# Revit family: Camera-Security-Panasonic-Super_Dynamic-Vandal_Resistant-Waterproof-Dome-Network-S2570LSeriesX
name_source: partatom
category: Security Devices
revit_build: Autodesk Revit 2016 (Build: 20150220_1215(x64)
units: mm (PartAtom-declared; Revit-internal decimal feet)

## family parameters
Cut with Voids When Loaded = No
Host = Face
Maintain Annotation Orientation = No
OmniClass Number = 23.85.10.14.11
OmniClass Title = Cameras
Part Type = Normal
Room Calculation Point = No
Round Connector Dimension = Use Diameter
Shared = No

## types (2) — shared parameters
4K = Resolution : 4K
Alarm Input Or Output Specification = ALARM IN 1(Alarm input 1/ Black & white input/ Auto time adjustment input) (x1), ALARM IN 2 (Alarm input 2/ ALARM OUT) (x1) , ALARM IN 3 (Alarm input 3/ AUX OUT) (x1)
Angle Of View = 101
Aspect169 = Yes
Audio In = Yes
Audio Out = Yes
Base Bracket Height = 1.417 "
Base Height = 2.205 "
Communication Ports = 10Base-T / 100Base-TX, RJ45 connector
Date Last Modified = 2019/05/14
Day Or Night = Yes
Decoration Cover Hole Radius = 1.634 "
Decoration Cover Wall Height = 0.118 "
Dome Bottom Offset = 0.197 "
Equipment Abbreviation = SC
Family Version = 1.0.0
Full HD = Resolution : Full HD
HD = Resolution : HD
HFOV Max 169 = 101.00°
HFOV Max 43 = 101.00°
HFOV Min 169 = 52.00°
HFOV Min 43 = 52.00°
Has POE = Yes
IP Or Analog = IP
Manufacturer = Panasonic
Minimum Illumination = 0.090 lx
Model Disclaimer = Contact Panasonic for more information
Product Documentation Link = https://bizpartner.panasonic.net
Product Page URL = https://security.panasonic.com
Provide Feedback = https://www.surveymonkey.com
Regulatory Compliance = UL (UL60950-1), c-UL (CSA C22.2 No.60950-1), CE, IEC60950-1, FCC (Part15 ClassA), ICES003 ClassA, EN55032 ClassB, EN55024
Tilt Max = 85.00°
Tilt Min = -30.00°
Tilting Range = -30 to +85
URL = http://security.panasonic.com
VFOV Max 169 = 55.00°
VFOV Max 43 = 55.00°
VFOV Min 169 = 29.00°
VFOV Min 43 = 29.00°
Vandal Resistant = Yes
Voltage DC = 12 V
WQHD = Resolution : WQHD
Wide Dynamic Range = Yes
Yaw Max = 100.00°
Yaw Min = -100.00°
Yawing Range = -100 to +100
z Const Pan Handle Length = 19.488 "
z Const Tilt Base Length = 9.843 "
z Const Tilt Base2 Length = 19.685 "
z Const Tilt Handle Length = 11.811 "
z Const Yaw Base Length = 10.236 "
z Const Yaw Base2 Length = 17.323 "
z Const Yaw Handle Length = 9.252 "
z Level Offset = 7.874 "
zero-valued in all types: Default Elevation, z Zero

## per-type parameters (varying)
- WV-S2570L: Base Radius=3.031 "; Decoration Cover Height=0.52 "; Decoration Cover Radius=4.14 "; Description=Security Camera, Fixed Dome, Network, Super Dynamic  Vandal Resistant  Weatherproof, 4K, WV-S2570L; Diameter=6.457 "; Dome Diameter=3.307 "; Height=5.472 "; Indoor Or Outdoor=Outdoor; Mounting Positions=Mount Dependent or Surface Mount; Operational Humidity=10 to 100 % (no condensation); Operational Temperature=-40 °F to 140 °F; Pan Max=180.00°; Pan Min=-180.00°; Panning Range=-180 to +180; Part Description=Security Camera, Fixed Dome, Network, Super Dynamic  Vandal Resistant  Weatherproof, 4K, WV-S2570L; Power Active=10.6 W; Product Material=Paint - Panasonic - Light Gray; Shock Resistance=50J (IEC 60068-2-75 compliant), IK10 (IEC 62262); Storage Temperature=-40 °F to 140 °F; Water and Dust Resistance=IP66 (IEC60529), Type 4X(UL50E), NEMA 4X compliant; z Camera Radius=3.027 "; z Camera Radius2=2.119 "; z Camera Type=1; z Dome Radius=1.654 "; z Embedded Bottom Offset=-1.685 "; z VV Viewpoint Depth Max=1.283 "; z VV Viewpoint Depth Min=1.283 "
- WV-S2270L: Base Radius=2.549 "; Decoration Cover Height=0.618 "; Decoration Cover Radius=3.661 "; Description=Security Camera, Fixed Dome, Network, Super Dynamic , 4K, WV-S2270L; Diameter=5.098 "; Dome Diameter=3.268 "; Height=4.035 "; Indoor Or Outdoor=Indoor; Mounting Positions=Surface Mount; Operational Humidity=10 to 90 % (no condensation); Operational Temperature=14 °F to 122 °F; Pan Max=120.00°; Pan Min=-240.00°; Panning Range=-240 to +120; Part Description=Security Camera, Fixed Dome, Network, Super Dynamic , 4K, WV-S2270L; Power Active=9.2 W; Product Material=Paint - Panasonic - Sail White; Shock Resistance=IK10 (IEC 62262); Storage Temperature=14 °F to 122 °F; z Camera Radius=2.549 "; z Camera Radius2=1.784 "; z Camera Type=0; z Dome Radius=1.634 "; z Embedded Bottom Offset=-1.673 "; z VV Viewpoint Depth Max=1.282 "; z VV Viewpoint Depth Min=1.282 "

note: column(s) folded — value = type name in every type: Model, Part Number

## geometry (parser evidence)
native form markers: Blend x4, Sweep x14
no freeform markers — native parametric forms only
